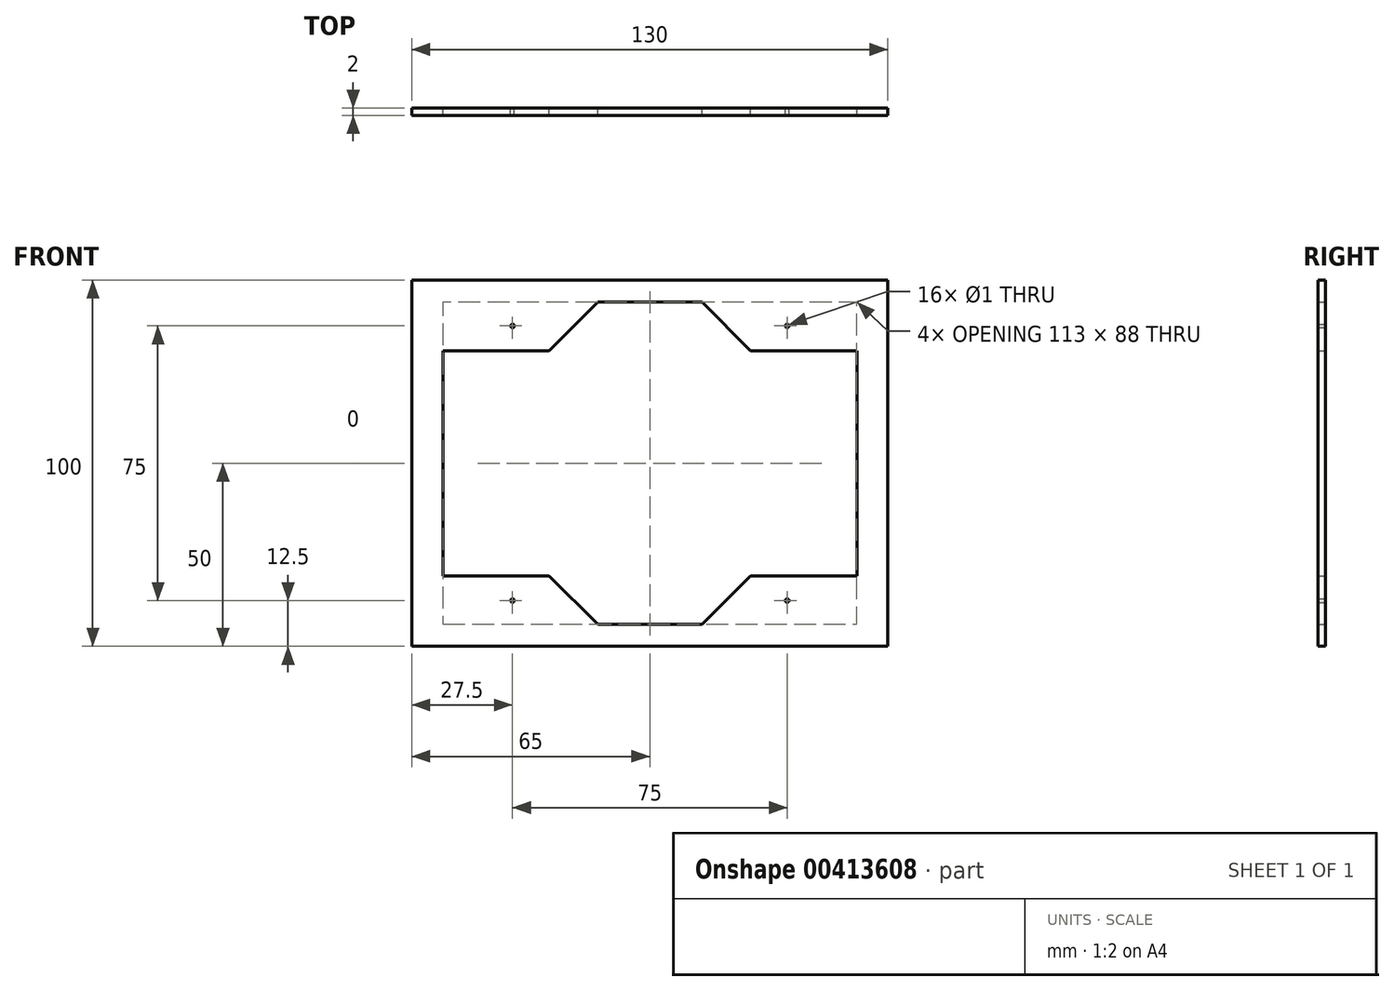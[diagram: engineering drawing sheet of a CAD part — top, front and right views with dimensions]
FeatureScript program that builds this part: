
annotation { "Feature Type Name" : "Feature", "Feature Type Description" : "" }
export const myFeature = defineFeature(function(context is Context, id is Id, definition is map)
    precondition{}
    {
        {
            var Q0;
            Q0=qCreatedBy(makeId("Front.planeOp"),FACE);
            var sketch = newSketch(context, id + "F0", { "sketchPlane" : qUnion([Q0])});
            skLineSegment(sketch, "E0.top", {"start": v(-14.24, 44) * mm, "end": v(0, 44) * mm});
            skLineSegment(sketch, "E0.left", {"start": v(-56.5, 0) * mm, "end": v(-56.5, 30.75) * mm});
            skPoint(sketch, "E0.middle", {"position": v(0, 0) * mm});
            skLineSegment(sketch, "E1.top", {"start": v(-56.5, 30.75) * mm, "end": v(-27.49, 30.75) * mm});
            skPoint(sketch, "E2", {"position": v(-37.5, 37.5) * mm});
            skLineSegment(sketch, "E3", {"start": v(-27.49, 30.75) * mm, "end": v(-14.24, 44) * mm});
            skPoint(sketch, "E4.orphan", {"position": v(-56.5, 44) * mm});
            skPoint(sketch, "E1.left.end.orphan", {"position": v(-52.75, 30.75) * mm});
            skPoint(sketch, "E1.bottom.start.orphan", {"position": v(-52.75, -30.75) * mm});
            skPoint(sketch, "E1.right.end.orphan", {"position": v(52.75, 30.75) * mm});
            skPoint(sketch, "E1.right.start.orphan", {"position": v(52.75, -30.75) * mm});
            skPoint(sketch, "E0.bottom.end.orphan", {"position": v(56.5, -44) * mm});
            skPoint(sketch, "E5.orphan", {"position": v(-56.5, -44) * mm});
            skPoint(sketch, "E6.orphan", {"position": v(56.5, 44) * mm});
            skLineSegment(sketch, "E7.MirrorCS", {"start": v(14.24, 44) * mm, "end": v(0, 44) * mm});
            skLineSegment(sketch, "E8.MirrorCS", {"start": v(27.49, 30.75) * mm, "end": v(14.24, 44) * mm});
            skLineSegment(sketch, "E9.MirrorCS", {"start": v(56.5, 30.75) * mm, "end": v(27.49, 30.75) * mm});
            skLineSegment(sketch, "E10.MirrorCS", {"start": v(56.5, 0) * mm, "end": v(56.5, 30.75) * mm});
            skPoint(sketch, "E11.MirrorP", {"position": v(37.5, 37.5) * mm});
            skLineSegment(sketch, "E12.MirrorCS", {"start": v(56.5, 0) * mm, "end": v(56.5, -30.75) * mm});
            skLineSegment(sketch, "E13.MirrorCS", {"start": v(-56.5, 0) * mm, "end": v(-56.5, -30.75) * mm});
            skLineSegment(sketch, "E14.MirrorCS", {"start": v(-27.49, -30.75) * mm, "end": v(-14.24, -44) * mm});
            skLineSegment(sketch, "E15.MirrorCS", {"start": v(-14.24, -44) * mm, "end": v(0, -44) * mm});
            skLineSegment(sketch, "E16.MirrorCS", {"start": v(56.5, -30.75) * mm, "end": v(27.49, -30.75) * mm});
            skLineSegment(sketch, "E17.MirrorCS", {"start": v(-56.5, -30.75) * mm, "end": v(-27.49, -30.75) * mm});
            skLineSegment(sketch, "E18.MirrorCS", {"start": v(27.49, -30.75) * mm, "end": v(14.24, -44) * mm});
            skLineSegment(sketch, "E19.MirrorCS", {"start": v(14.24, -44) * mm, "end": v(0, -44) * mm});
            skPoint(sketch, "E20.MirrorP", {"position": v(37.5, -37.5) * mm});
            skPoint(sketch, "E21.MirrorP", {"position": v(-37.5, -37.5) * mm});
            skLineSegment(sketch, "E22.bottom", {"start": v(-65, -50) * mm, "end": v(65, -50) * mm});
            skLineSegment(sketch, "E22.top", {"start": v(-65, 50) * mm, "end": v(65, 50) * mm});
            skLineSegment(sketch, "E22.left", {"start": v(-65, -50) * mm, "end": v(-65, 50) * mm});
            skLineSegment(sketch, "E22.right", {"start": v(65, -50) * mm, "end": v(65, 50) * mm});
            skCircle(sketch, "E23", {"center": v(-37.5, 37.5) * mm, "radius": 0.5 * mm});
            skCircle(sketch, "E24", {"center": v(37.5, -37.5) * mm, "radius": 0.5 * mm});
            skCircle(sketch, "E25", {"center": v(-37.5, -37.5) * mm, "radius": 0.5 * mm});
            skCircle(sketch, "E26", {"center": v(37.5, 37.5) * mm, "radius": 0.5 * mm});
            skSolve(sketch);
        }
        {
            var Q0;
            Q0 = qSketchRegion(id + "F0", true);
            extrude(context, id + "F1", {"entities" : qUnion([Q0]), "depth" : 2 * mm});
        }
    });
